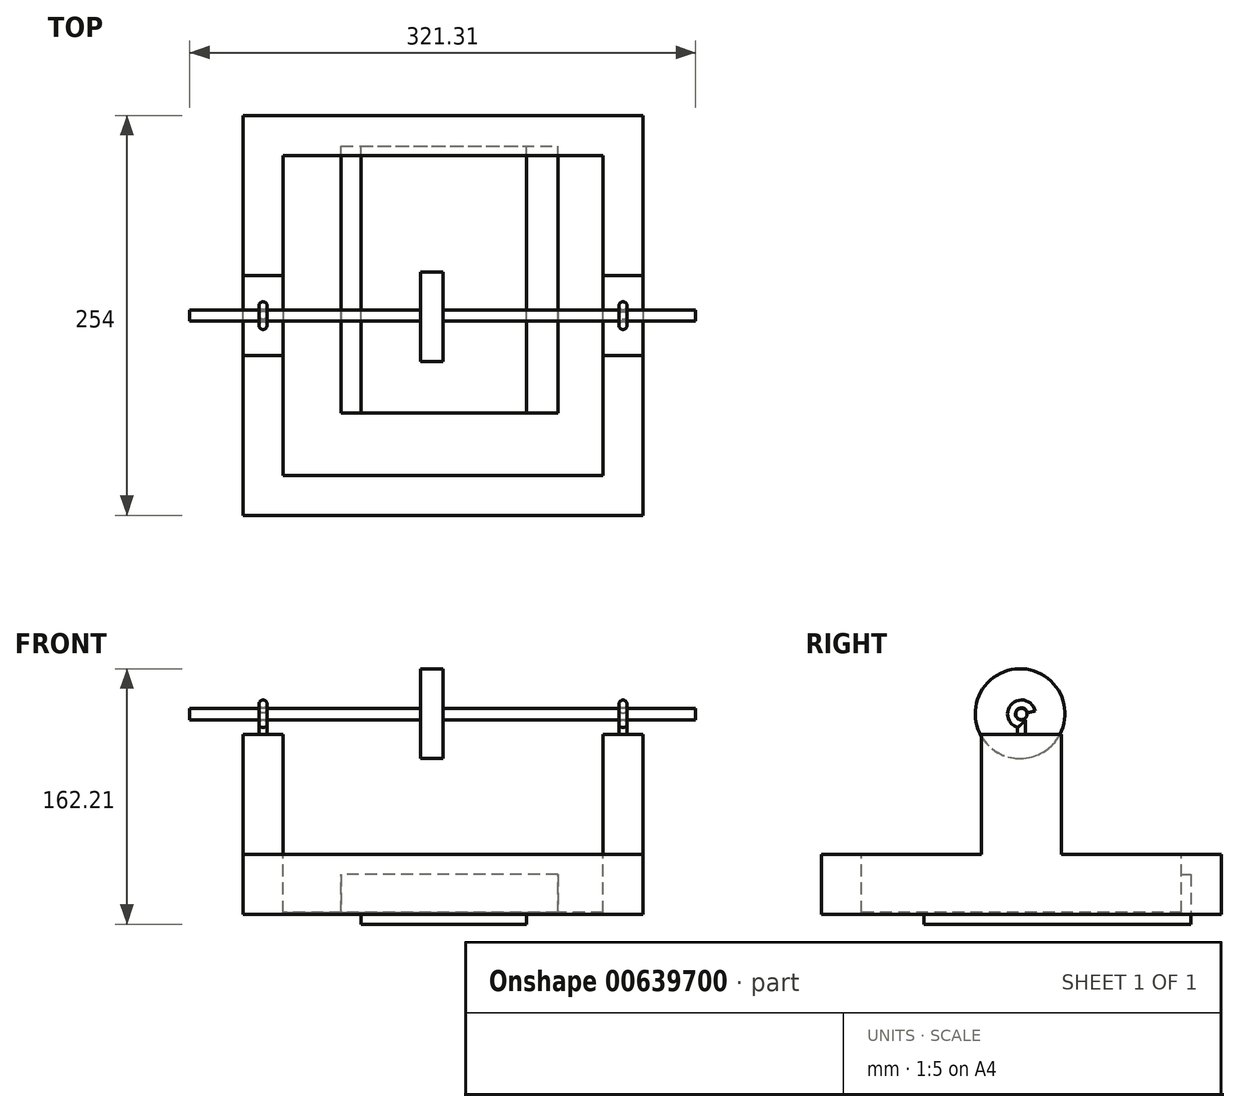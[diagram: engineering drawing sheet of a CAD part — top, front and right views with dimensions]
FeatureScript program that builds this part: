
annotation { "Feature Type Name" : "Feature", "Feature Type Description" : "" }
export const myFeature = defineFeature(function(context is Context, id is Id, definition is map)
    precondition{}
    {
        {
            var Q0;
            Q0=qCreatedBy(makeId("Top.planeOp"),FACE);
            var sketch = newSketch(context, id + "F0", { "sketchPlane" : qUnion([Q0])});
            skLineSegment(sketch, "E0", {"start": v(0, 0) * mm, "end": v(0, 254) * mm});
            skLineSegment(sketch, "E1", {"start": v(0, 254) * mm, "end": v(254, 254) * mm});
            skLineSegment(sketch, "E2", {"start": v(254, 254) * mm, "end": v(254, 0) * mm});
            skLineSegment(sketch, "E3", {"start": v(254, 0) * mm, "end": v(0, 0) * mm});
            skSolve(sketch);
        }
        {
            var Q0;
            Q0=makeQuery(id+"F0.imprint","IMPRINT",FACE,{"disambiguationData":[TD([[makeQuery(id+"F0.imprint","IMPRINT",EDGE,{"derivedFrom":sQuery(id+"F0.wireOp",EDGE,"E0")}),-1.0]])]});
            extrude(context, id + "F1", {"entities" : qUnion([Q0]), "depth" : 38.1 * mm, "offsetDistance" : 25.4 * mm});
        }
        {
            var Q0;
            Q0=makeQuery(id+"F1.opExtrude","CAP_FACE",FACE,{"disambiguationData":[OSD([sQuery(id+"F0.wireOp",EDGE,"E0"),sQuery(id+"F0.wireOp",EDGE,"E1"),sQuery(id+"F0.wireOp",EDGE,"E2"),sQuery(id+"F0.wireOp",EDGE,"E3")])],"isStart":false});
            var sketch = newSketch(context, id + "F2", { "sketchPlane" : qUnion([Q0])});
            skLineSegment(sketch, "E4", {"start": v(25.4, 228.6) * mm, "end": v(25.4, 25.4) * mm});
            skLineSegment(sketch, "E5", {"start": v(25.4, 25.4) * mm, "end": v(228.6, 25.4) * mm});
            skLineSegment(sketch, "E6", {"start": v(228.6, 25.4) * mm, "end": v(228.6, 228.6) * mm});
            skLineSegment(sketch, "E7", {"start": v(228.6, 228.6) * mm, "end": v(25.4, 228.6) * mm});
            skSolve(sketch);
        }
        {
            var Q0;
            Q0=makeQuery(id+"F2.imprint","IMPRINT",FACE,{"disambiguationData":[TD([[makeQuery(id+"F2.imprint","IMPRINT",EDGE,{"derivedFrom":sQuery(id+"F2.wireOp",EDGE,"E4")}),1.0]])]});
            extrude(context, id + "F3", {"entities" : qUnion([Q0]), "operationType" : NewBodyOperationType.REMOVE, "oppositeDirection" : true, "depth" : 36.83 * mm, "offsetDistance" : 25.4 * mm});
        }
        {
            var Q0;
            Q0=makeQuery(id+"F1.opExtrude","CAP_FACE",FACE,{"disambiguationData":[OSD([sQuery(id+"F0.wireOp",EDGE,"E0"),sQuery(id+"F0.wireOp",EDGE,"E1"),sQuery(id+"F0.wireOp",EDGE,"E2"),sQuery(id+"F0.wireOp",EDGE,"E3")])],"isStart":false});
            var sketch = newSketch(context, id + "F4", { "sketchPlane" : qUnion([Q0])});
            skLineSegment(sketch, "E8.bottom", {"start": v(25.4, 101.6) * mm, "end": v(0, 101.6) * mm});
            skLineSegment(sketch, "E8.top", {"start": v(25.4, 152.4) * mm, "end": v(0, 152.4) * mm});
            skLineSegment(sketch, "E8.left", {"start": v(25.4, 101.6) * mm, "end": v(25.4, 152.4) * mm});
            skLineSegment(sketch, "E8.right", {"start": v(0, 101.6) * mm, "end": v(0, 152.4) * mm});
            skPoint(sketch, "E9.firstSnap0", {"position": v(12.7, 152.4) * mm});
            skLineSegment(sketch, "E9.bottom", {"start": v(228.6, 152.4) * mm, "end": v(254, 152.4) * mm});
            skLineSegment(sketch, "E9.top", {"start": v(228.6, 101.6) * mm, "end": v(254, 101.6) * mm});
            skLineSegment(sketch, "E9.left", {"start": v(228.6, 152.4) * mm, "end": v(228.6, 101.6) * mm});
            skLineSegment(sketch, "E9.right", {"start": v(254, 152.4) * mm, "end": v(254, 101.6) * mm});
            skSolve(sketch);
        }
        {
            var Q0;
            Q0=makeQuery(id+"F4.imprint","IMPRINT",FACE,{"disambiguationData":[TD([[makeQuery(id+"F4.imprint","IMPRINT",EDGE,{"derivedFrom":sQuery(id+"F4.wireOp",EDGE,"E9.bottom")}),-1.0]])]});
            var Q1;
            Q1=makeQuery(id+"F4.imprint","IMPRINT",FACE,{"disambiguationData":[TD([[makeQuery(id+"F4.imprint","IMPRINT",EDGE,{"derivedFrom":sQuery(id+"F4.wireOp",EDGE,"E8.bottom")}),-1.0]])]});
            extrude(context, id + "F5", {"entities" : qUnion([Q0, Q1]), "operationType" : NewBodyOperationType.ADD, "depth" : 76.2 * mm, "offsetDistance" : 25.4 * mm});
        }
        {
            var Q0;
            Q0=makeQuery(id+"F5.opExtrude","CAP_FACE",FACE,{"disambiguationData":[OSD([sQuery(id+"F4.wireOp",EDGE,"E8.bottom"),sQuery(id+"F4.wireOp",EDGE,"E8.top"),sQuery(id+"F4.wireOp",EDGE,"E8.left"),sQuery(id+"F4.wireOp",EDGE,"E8.right")])],"isStart":false});
            var sketch = newSketch(context, id + "F6", { "sketchPlane" : qUnion([Q0])});
            skCircle(sketch, "E10", {"center": v(12.7, 127) * mm, "radius": 2.54 * mm});
            skPoint(sketch, "E10.centerSnap0", {"position": v(12.7, 152.4) * mm});
            skPoint(sketch, "E10.centerSnap1", {"position": v(0, 127) * mm});
            skSolve(sketch);
        }
        {
            var Q0;
            Q0=makeQuery(id+"F5.opExtrude","CAP_EDGE",EDGE,{"disambiguationData":[OSD([sQuery(id+"F4.wireOp",EDGE,"E8.bottom")])],"isStart":false});
            cPoint(context, id + "F7", {"entities" : qUnion([Q0]), "parameter" : 0.5});
        }
        {
            var Q0;
            Q0=qCreatedBy(makeId("Right.planeOp"),FACE);
            var Q1;
            Q1 = qCreatedBy(id + "F7" ,VERTEX);
            cPlane(context, id + "F8", {"entities" : qUnion([Q0, Q1]), "cplaneType" : CPlaneType.PLANE_POINT, "offset" : 25.4 * mm, "width" : 152.4 * mm, "height" : 152.4 * mm});
        }
        {
            var Q0;
            Q0=qCreatedBy(id+"F8.planeOp",FACE);
            var sketch = newSketch(context, id + "F9", { "sketchPlane" : qUnion([Q0])});
            skLineSegment(sketch, "E11.0", {"start": v(124.46, 114.3) * mm, "end": v(129.54, 114.3) * mm});
            skLineSegment(sketch, "E12", {"start": v(127, 114.3) * mm, "end": v(127, 121.05) * mm});
            skArc(sketch, "E13", {"start": v(127, 121.05) * mm, "mid": v(121.93, 131.36) * mm, "end": v(133.11, 128.7) * mm});
            skSolve(sketch);
        }
        {
            var Q0;
            Q0=makeQuery(id+"F6.imprint","IMPRINT",FACE,{"disambiguationData":[TD([[makeQuery(id+"F6.imprint","IMPRINT",EDGE,{"derivedFrom":sQuery(id+"F6.wireOp",EDGE,"E10")}),1.0]])]});
            var Q1;
            Q1 = qSketchRegion(id + "F9", true);
            var Q2;
            Q2=sQuery(id+"F9.wireOp",EDGE,"E12");
            var Q3;
            Q3=sQuery(id+"F9.wireOp",EDGE,"E13");
            sweep(context, id + "F10", {"profiles" : qUnion([Q0, Q1]), "path" : qUnion([Q2, Q3])});
        }
        {
            var Q0;
            Q0=makeQuery(id+"F1.opExtrude","CAP_EDGE",EDGE,{"disambiguationData":[OSD([sQuery(id+"F0.wireOp",EDGE,"E3")])],"isStart":false});
            cPoint(context, id + "F11", {"entities" : qUnion([Q0]), "parameter" : 0.5});
        }
        {
            var Q0;
            Q0=qCreatedBy(makeId("Right.planeOp"),FACE);
            var Q1;
            Q1 = qCreatedBy(id + "F11" ,VERTEX);
            cPlane(context, id + "F12", {"entities" : qUnion([Q0, Q1]), "cplaneType" : CPlaneType.PLANE_POINT, "offset" : 25.4 * mm, "width" : 152.4 * mm, "height" : 152.4 * mm});
        }
        {
            var Q0;
            Q0=makeQuery(id+"F10.opSweep","SWEPT_BODY",BODY,{"disambiguationData":[OSD([sQuery(id+"F6.wireOp",EDGE,"E10"),sQuery(id+"F9.wireOp",EDGE,"E13")])]});
            var Q1;
            Q1=qCreatedBy(id+"F12.planeOp",FACE);
            mirror(context, id + "F13", {"operationType" : NewBodyOperationType.ADD, "entities" : qUnion([Q0]), "mirrorPlane" : qUnion([Q1])});
        }
        {
            var Q0;
            Q0=qCreatedBy(id+"F8.planeOp",FACE);
            var sketch = newSketch(context, id + "F14", { "sketchPlane" : qUnion([Q0])});
            skCircle(sketch, "E14", {"center": v(126.83, 127.34) * mm, "radius": 3.6 * mm});
            skSolve(sketch);
        }
        {
            var Q0;
            Q0=makeQuery(id+"F14.imprint","IMPRINT",FACE,{"disambiguationData":[TD([[makeQuery(id+"F14.imprint","IMPRINT",EDGE,{"derivedFrom":sQuery(id+"F14.wireOp",EDGE,"E14")}),1.0]])]});
            extrude(context, id + "F15", {"entities" : qUnion([Q0]), "depth" : 274.83 * mm, "offsetDistance" : 25.4 * mm});
        }
        {
            var Q0;
            Q0=makeQuery(id+"F15.opExtrude","CAP_FACE",FACE,{"disambiguationData":[OSD([sQuery(id+"F14.wireOp",EDGE,"E14")])],"isStart":true});
            extrude(context, id + "F16", {"entities" : qUnion([Q0]), "operationType" : NewBodyOperationType.ADD, "depth" : 46.48 * mm, "offsetDistance" : 25.4 * mm});
        }
        {
            var Q0;
            Q0=qCreatedBy(id+"F12.planeOp",FACE);
            var sketch = newSketch(context, id + "F17", { "sketchPlane" : qUnion([Q0])});
            skCircle(sketch, "E15", {"center": v(126.02, 127.6) * mm, "radius": 28.51 * mm});
            skSolve(sketch);
        }
        {
            var Q0;
            Q0 = qSketchRegion(id + "F17", true);
            extrude(context, id + "F18", {"entities" : qUnion([Q0]), "operationType" : NewBodyOperationType.ADD, "oppositeDirection" : true, "depth" : 14.22 * mm, "offsetDistance" : 25.4 * mm});
        }
        {
            var Q0;
            Q0=makeQuery(id+"F1.opExtrude","CAP_FACE",FACE,{"disambiguationData":[OSD([sQuery(id+"F0.wireOp",EDGE,"E0"),sQuery(id+"F0.wireOp",EDGE,"E1"),sQuery(id+"F0.wireOp",EDGE,"E2"),sQuery(id+"F0.wireOp",EDGE,"E3")])],"isStart":true});
            var sketch = newSketch(context, id + "F19", { "sketchPlane" : qUnion([Q0])});
            skLineSegment(sketch, "E16.bottom", {"start": v(62.4, -64.9) * mm, "end": v(199.98, -64.9) * mm});
            skLineSegment(sketch, "E16.top", {"start": v(62.4, -234.4) * mm, "end": v(199.98, -234.4) * mm});
            skLineSegment(sketch, "E16.left", {"start": v(62.4, -64.9) * mm, "end": v(62.4, -234.4) * mm});
            skLineSegment(sketch, "E16.right", {"start": v(199.98, -64.9) * mm, "end": v(199.98, -234.4) * mm});
            skSolve(sketch);
        }
        {
            var Q0;
            Q0=makeQuery(id+"F19.imprint","IMPRINT",FACE,{"disambiguationData":[TD([[makeQuery(id+"F19.imprint","IMPRINT",EDGE,{"derivedFrom":sQuery(id+"F19.wireOp",EDGE,"E16.bottom")}),-1.0]])]});
            extrude(context, id + "F20", {"entities" : qUnion([Q0]), "operationType" : NewBodyOperationType.REMOVE, "oppositeDirection" : true, "depth" : 25.4 * mm, "offsetDistance" : 25.4 * mm});
        }
        {
            var Q0;
            Q0=makeQuery(id+"F1.opExtrude","CAP_FACE",FACE,{"disambiguationData":[OSD([sQuery(id+"F0.wireOp",EDGE,"E0"),sQuery(id+"F0.wireOp",EDGE,"E1"),sQuery(id+"F0.wireOp",EDGE,"E2"),sQuery(id+"F0.wireOp",EDGE,"E3")])],"isStart":true});
            var sketch = newSketch(context, id + "F21", { "sketchPlane" : qUnion([Q0])});
            skLineSegment(sketch, "E17.bottom", {"start": v(75.05, -64.9) * mm, "end": v(180.17, -64.9) * mm});
            skLineSegment(sketch, "E17.top", {"start": v(75.05, -234.4) * mm, "end": v(180.17, -234.4) * mm});
            skLineSegment(sketch, "E17.left", {"start": v(75.05, -64.9) * mm, "end": v(75.05, -234.4) * mm});
            skLineSegment(sketch, "E17.right", {"start": v(180.17, -64.9) * mm, "end": v(180.17, -234.4) * mm});
            skSolve(sketch);
        }
        {
            var Q0;
            Q0 = qSketchRegion(id + "F21", true);
            extrude(context, id + "F22", {"entities" : qUnion([Q0]), "depth" : 6.1 * mm, "offsetDistance" : 25.4 * mm});
        }
    });
